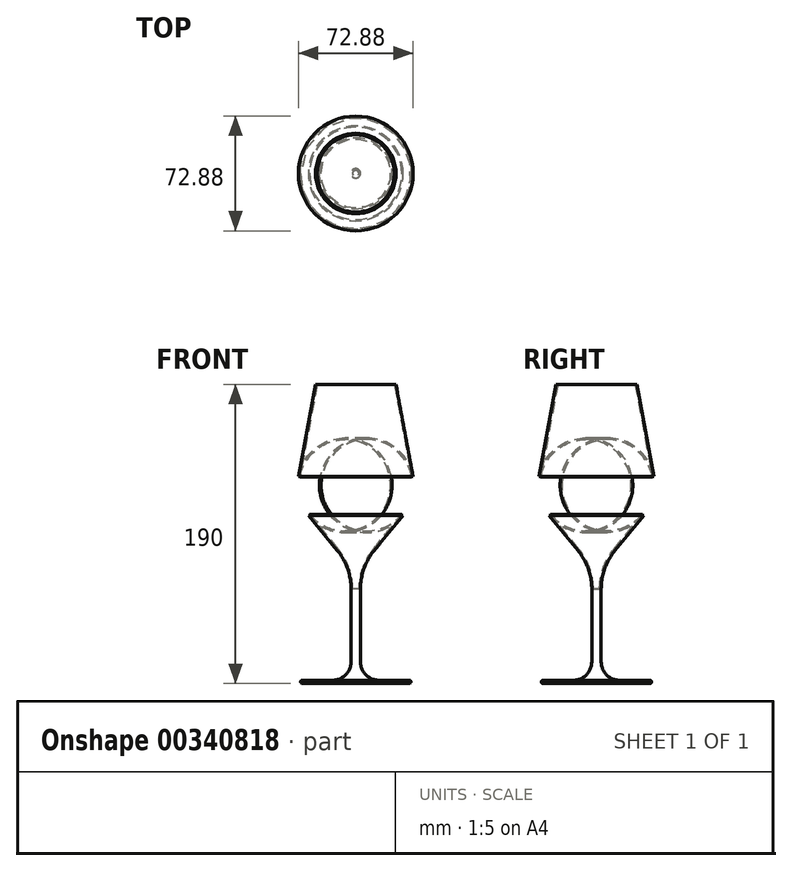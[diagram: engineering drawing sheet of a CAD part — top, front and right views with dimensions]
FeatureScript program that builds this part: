
annotation { "Feature Type Name" : "Feature", "Feature Type Description" : "" }
export const myFeature = defineFeature(function(context is Context, id is Id, definition is map)
    precondition{}
    {
        {
            var Q0;
            Q0=qCreatedBy(makeId("Front.planeOp"),FACE);
            var sketch = newSketch(context, id + "F0", { "sketchPlane" : qUnion([Q0])});
            skLineSegment(sketch, "E0", {"start": v(35, 0) * mm, "end": v(35, 2) * mm});
            skLineSegment(sketch, "E1", {"start": v(35, 2) * mm, "end": v(14.67, 2) * mm});
            skArc(sketch, "E2", {"start": v(3, 13.67) * mm, "mid": v(6.42, 5.42) * mm, "end": v(14.67, 2) * mm});
            skLineSegment(sketch, "E3", {"start": v(3, 13.67) * mm, "end": v(3, 60) * mm});
            skArc(sketch, "E4", {"start": v(11.8, 84.56) * mm, "mid": v(5.27, 73.04) * mm, "end": v(3, 60) * mm});
            skLineSegment(sketch, "E5", {"start": v(11.8, 84.56) * mm, "end": v(30.12, 106.84) * mm});
            skArc(sketch, "E6", {"start": v(30.12, 106.84) * mm, "mid": v(36, 118.4) * mm, "end": v(36.44, 131.37) * mm});
            skLineSegment(sketch, "E7", {"start": v(36.44, 131.37) * mm, "end": v(25.56, 190) * mm});
            skLineSegment(sketch, "E8", {"start": v(25.56, 190) * mm, "end": v(24.55, 190) * mm});
            skLineSegment(sketch, "E9", {"start": v(35, 0) * mm, "end": v(0, 0) * mm});
            skLineSegment(sketch, "E10.0", {"start": v(35.46, 131.19) * mm, "end": v(24.72, 189.09) * mm});
            skArc(sketch, "E10.1", {"start": v(29.35, 107.48) * mm, "mid": v(35.03, 118.66) * mm, "end": v(35.46, 131.19) * mm});
            skLineSegment(sketch, "E10.2", {"start": v(11.03, 85.2) * mm, "end": v(29.35, 107.48) * mm});
            skArc(sketch, "E10.3", {"start": v(11.03, 85.2) * mm, "mid": v(4.32, 73.38) * mm, "end": v(2, 60) * mm});
            skLineSegment(sketch, "E11", {"start": v(24.72, 189.09) * mm, "end": v(24.55, 190) * mm});
            skLineSegment(sketch, "E12.trimOffspring", {"start": v(0, 0) * mm, "end": v(0, -36.9) * mm, "construction": true});
            skLineSegment(sketch, "E13", {"start": v(2, 60) * mm, "end": v(0, 60) * mm});
            skLineSegment(sketch, "E14", {"start": v(0, 60) * mm, "end": v(0, 0) * mm});
            skSolve(sketch);
        }
        {
            var Q0;
            Q0 = qSketchRegion(id + "F0", true);
            var Q1;
            Q1 = qConstructionFilter(qBodyType(qCreatedBy(id + "F0" ,EDGE), BodyType.WIRE), ConstructionObject.NO);
            var Q2;
            Q2=sQuery(id+"F0.wireOp",EDGE,"E12.trimOffspring");
            revolve(context, id + "F1", {"entities" : qUnion([Q0]), "surfaceEntities" : qUnion([Q1]), "axis" : qUnion([Q2]), "revolveType" : RevolveType.FULL});
        }
        {
            var Q0;
            Q0=makeQuery(id+"F1.opRevolve","SWEPT_EDGE",EDGE,{"disambiguationData":[OSD([sQuery(id+"F0.wireOp",EDGE,"E0"),sQuery(id+"F0.wireOp",EDGE,"E1")])]});
            fillet(context, id + "F2", {"entities" : qUnion([Q0]), "radius" : 1 * mm, "tangentPropagation" : true, "allowEdgeOverflow" : false});
        }
        {
            var Q0;
            Q0=makeQuery(id+"F1.opRevolve","SWEPT_EDGE",EDGE,{"disambiguationData":[OSD([sQuery(id+"F0.wireOp",EDGE,"E0"),sQuery(id+"F0.wireOp",EDGE,"E9")])]});
            fillet(context, id + "F3", {"entities" : qUnion([Q0]), "radius" : 1 * mm, "tangentPropagation" : true, "allowEdgeOverflow" : false});
        }
    });
